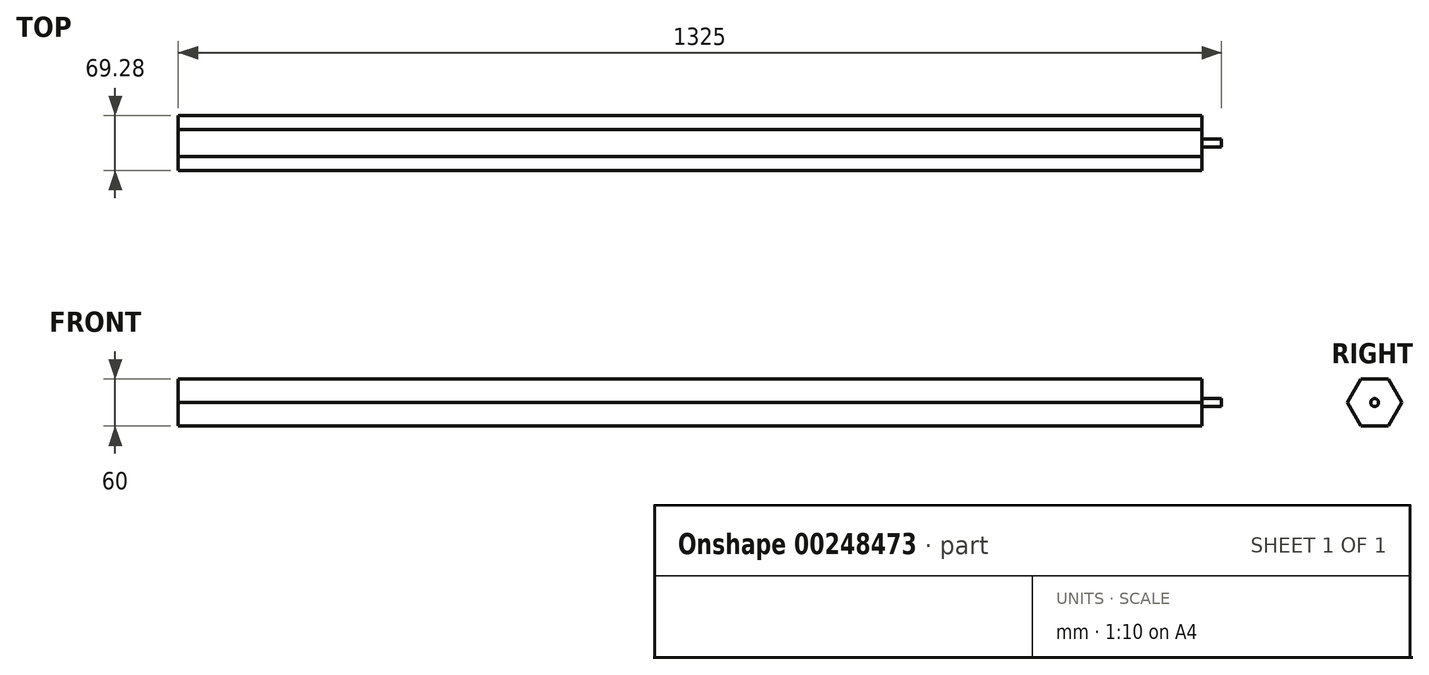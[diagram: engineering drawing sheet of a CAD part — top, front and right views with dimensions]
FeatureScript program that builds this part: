
annotation { "Feature Type Name" : "Feature", "Feature Type Description" : "" }
export const myFeature = defineFeature(function(context is Context, id is Id, definition is map)
    precondition{}
    {
        {
            var Q0;
            Q0=qCreatedBy(makeId("Right.planeOp"),FACE);
            var sketch = newSketch(context, id + "F0", { "sketchPlane" : qUnion([Q0])});
            skCircle(sketch, "E0.cCircle", {"center": v(0, 0) * mm, "radius": 30 * mm, "construction": true});
            skLineSegment(sketch, "E0.0", {"start": v(17.32, -30) * mm, "end": v(-17.32, -30) * mm});
            skLineSegment(sketch, "E0.1", {"start": v(-17.32, -30) * mm, "end": v(-34.64, 0) * mm});
            skLineSegment(sketch, "E0.2", {"start": v(-34.64, 0) * mm, "end": v(-17.32, 30) * mm});
            skLineSegment(sketch, "E0.3", {"start": v(-17.32, 30) * mm, "end": v(17.32, 30) * mm});
            skLineSegment(sketch, "E0.4", {"start": v(17.32, 30) * mm, "end": v(34.64, 0) * mm});
            skLineSegment(sketch, "E0.5", {"start": v(34.64, 0) * mm, "end": v(17.32, -30) * mm});
            skPoint(sketch, "E0.0.midPoint", {"position": v(0, -30) * mm});
            skSolve(sketch);
        }
        {
            var Q0;
            Q0 = qSketchRegion(id + "F0", true);
            extrude(context, id + "F1", {"entities" : qUnion([Q0]), "depth" : 1300 * mm});
        }
        {
            var Q0;
            Q0=makeQuery(id+"F1.opExtrude","CAP_FACE",FACE,{"disambiguationData":[OSD([sQuery(id+"F0.wireOp",EDGE,"E0.0"),sQuery(id+"F0.wireOp",EDGE,"E0.1"),sQuery(id+"F0.wireOp",EDGE,"E0.2"),sQuery(id+"F0.wireOp",EDGE,"E0.3"),sQuery(id+"F0.wireOp",EDGE,"E0.4"),sQuery(id+"F0.wireOp",EDGE,"E0.5")])],"isStart":false});
            var sketch = newSketch(context, id + "F2", { "sketchPlane" : qUnion([Q0])});
            skCircle(sketch, "E1", {"center": v(0, 0) * mm, "radius": 5 * mm});
            skSolve(sketch);
        }
        {
            var Q0;
            Q0 = qSketchRegion(id + "F2", true);
            extrude(context, id + "F3", {"entities" : qUnion([Q0]), "operationType" : NewBodyOperationType.ADD, "depth" : 25 * mm});
        }
    });
